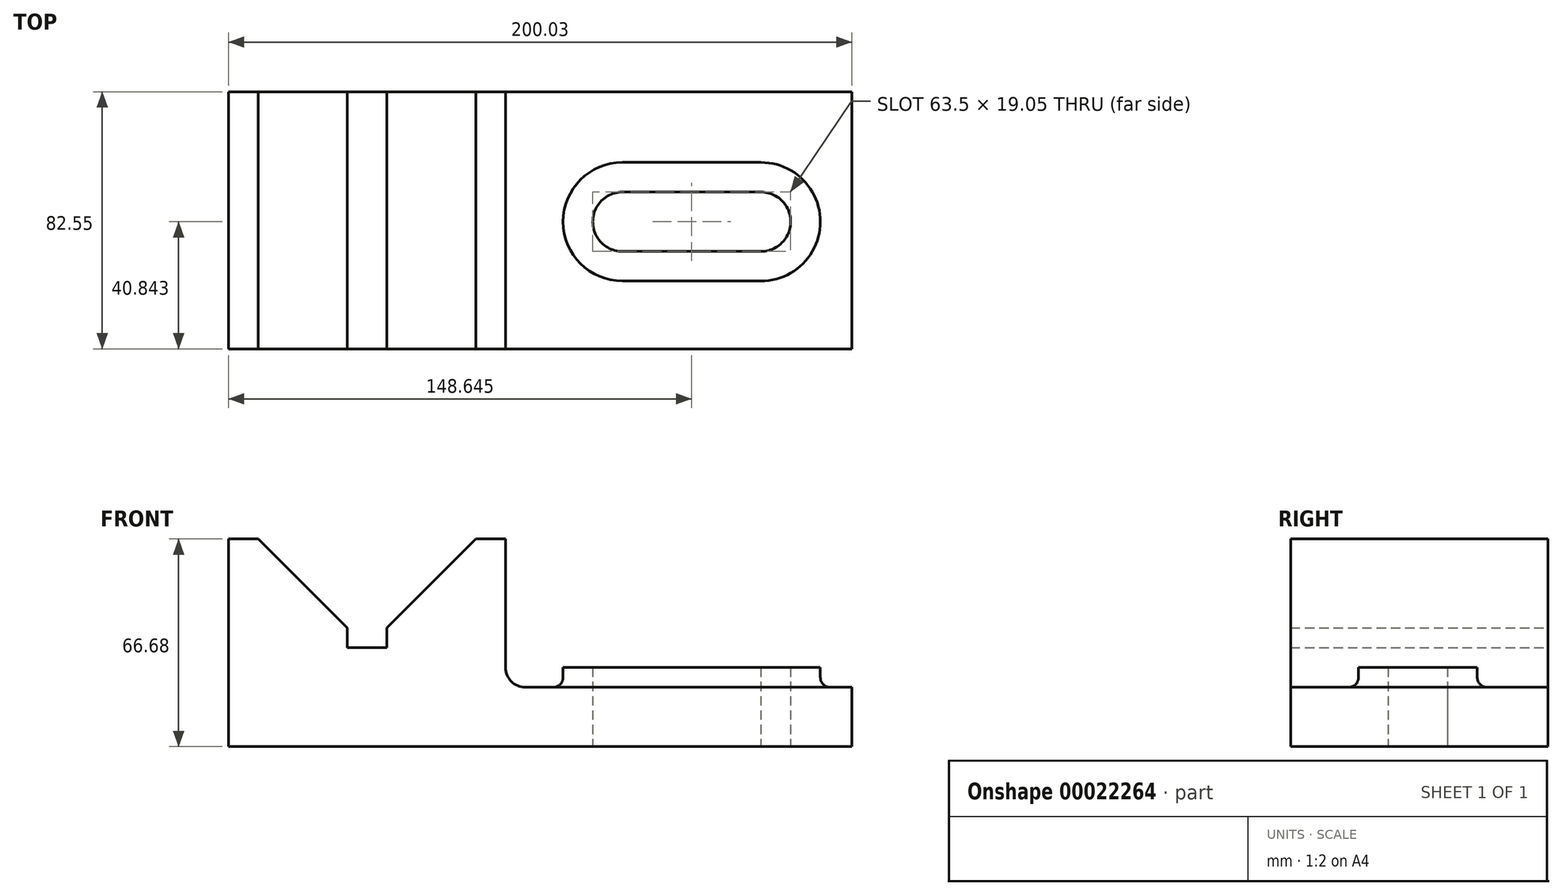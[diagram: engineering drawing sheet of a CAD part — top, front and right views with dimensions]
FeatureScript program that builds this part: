
annotation { "Feature Type Name" : "Feature", "Feature Type Description" : "" }
export const myFeature = defineFeature(function(context is Context, id is Id, definition is map)
    precondition{}
    {
        {
            var Q0;
            Q0=qCreatedBy(makeId("Front.planeOp"),FACE);
            var sketch = newSketch(context, id + "F0", { "sketchPlane" : qUnion([Q0])});
            skLineSegment(sketch, "E0.bottom", {"start": v(0, 0) * mm, "end": v(-200.03, 0) * mm});
            skLineSegment(sketch, "E0.left", {"start": v(0, 0) * mm, "end": v(0, 19.05) * mm});
            skLineSegment(sketch, "E0.right", {"start": v(-200.03, 0) * mm, "end": v(-200.03, 66.68) * mm});
            skLineSegment(sketch, "E1", {"start": v(-111.12, 66.68) * mm, "end": v(-111.12, 25.4) * mm});
            skLineSegment(sketch, "E2", {"start": v(-104.77, 19.05) * mm, "end": v(0, 19.05) * mm});
            skPoint(sketch, "E3.orphan", {"position": v(0, 57.15) * mm});
            skArc(sketch, "E4", {"start": v(-111.12, 25.4) * mm, "mid": v(-109.27, 20.9) * mm, "end": v(-104.77, 19.05) * mm});
            skLineSegment(sketch, "E5", {"start": v(-200.03, 66.68) * mm, "end": v(-190.5, 66.68) * mm});
            skLineSegment(sketch, "E6", {"start": v(-190.5, 66.68) * mm, "end": v(-161.93, 38.1) * mm});
            skLineSegment(sketch, "E7", {"start": v(-120.65, 66.68) * mm, "end": v(-149.23, 38.1) * mm});
            skLineSegment(sketch, "E8", {"start": v(-155.58, 31.75) * mm, "end": v(-149.23, 31.75) * mm});
            skLineSegment(sketch, "E9", {"start": v(-149.23, 31.75) * mm, "end": v(-161.93, 31.75) * mm});
            skLineSegment(sketch, "E10", {"start": v(-161.93, 31.75) * mm, "end": v(-161.93, 38.1) * mm});
            skLineSegment(sketch, "E11", {"start": v(-149.23, 31.75) * mm, "end": v(-149.23, 38.1) * mm});
            skLineSegment(sketch, "E12.trimOffspring", {"start": v(-120.65, 66.68) * mm, "end": v(-111.12, 66.68) * mm});
            skSolve(sketch);
        }
        {
            var Q0;
            Q0 = qSketchRegion(id + "F0", true);
            var Q1;
            Q1=makeQuery(id+"F0.imprint","IMPRINT",FACE,{"disambiguationData":[TD([[makeQuery(id+"F0.imprint","IMPRINT",EDGE,{"derivedFrom":sQuery(id+"F0.wireOp",EDGE,"E0.bottom")}),-1.0]])]});
            extrude(context, id + "F1", {"entities" : qUnion([Q0, Q1]), "depth" : 82.55 * mm});
        }
        {
            var Q0;
            Q0=makeQuery(id+"F1.opExtrude","SWEPT_FACE",FACE,{"disambiguationData":[OSD([sQuery(id+"F0.wireOp",EDGE,"E2")])]});
            var sketch = newSketch(context, id + "F2", { "sketchPlane" : qUnion([Q0])});
            skArc(sketch, "E13", {"start": v(-73.6, -22.66) * mm, "mid": v(-92.66, -41.7) * mm, "end": v(-73.6, -60.76) * mm});
            skPoint(sketch, "E14.center.orphan", {"position": v(-29.16, -41.7) * mm});
            skArc(sketch, "E15", {"start": v(-29.16, -60.76) * mm, "mid": v(-10.1, -41.7) * mm, "end": v(-29.16, -22.66) * mm});
            skLineSegment(sketch, "E16", {"start": v(-29.16, -60.76) * mm, "end": v(-73.6, -60.76) * mm});
            skLineSegment(sketch, "E17", {"start": v(-73.6, -22.66) * mm, "end": v(-29.16, -22.66) * mm});
            skArc(sketch, "E18", {"start": v(-73.6, -32.18) * mm, "mid": v(-83.13, -41.73) * mm, "end": v(-73.57, -51.23) * mm});
            skArc(sketch, "E19", {"start": v(-29.2, -51.23) * mm, "mid": v(-19.63, -41.68) * mm, "end": v(-29.26, -32.18) * mm});
            skLineSegment(sketch, "E20", {"start": v(-29.2, -51.23) * mm, "end": v(-73.65, -51.23) * mm});
            skLineSegment(sketch, "E21", {"start": v(-29.05, -32.18) * mm, "end": v(-73.6, -32.18) * mm});
            skPoint(sketch, "E22.trimOffspring.end.orphan", {"position": v(-104.78, -41.7) * mm});
            skPoint(sketch, "E23.start.orphan", {"position": v(0, -41.28) * mm});
            skSolve(sketch);
        }
        {
            var Q0;
            Q0=makeQuery(id+"F2.imprint","IMPRINT",FACE,{"disambiguationData":[TD([[makeQuery(id+"F2.imprint","IMPRINT",EDGE,{"derivedFrom":sQuery(id+"F2.wireOp",EDGE,"E13")}),1.0]])]});
            extrude(context, id + "F3", {"entities" : qUnion([Q0]), "operationType" : NewBodyOperationType.ADD, "depth" : 6.35 * mm});
        }
        {
            var Q0;
            Q0=makeQuery(id+"F3.opExtrude","CAP_EDGE",EDGE,{"disambiguationData":[OSD([sQuery(id+"F2.wireOp",EDGE,"E15")])],"isStart":true});
            fillet(context, id + "F4", {"entities" : qUnion([Q0]), "radius" : 3.17 * mm, "tangentPropagation" : true, "allowEdgeOverflow" : false});
        }
        {
            var Q0;
            Q0=makeQuery(id+"F3.boolean.opBoolean","SPLIT",FACE,{"disambiguationData":[TD([makeQuery(id+"F3.opExtrude","SWEPT_FACE",FACE,{"disambiguationData":[OSD([sQuery(id+"F2.wireOp",EDGE,"E18")])]})])],"derivedFrom":makeQuery(id+"F1.opExtrude","SWEPT_FACE",FACE,{"disambiguationData":[OSD([sQuery(id+"F0.wireOp",EDGE,"E2")])]})});
            extrude(context, id + "F5", {"entities" : qUnion([Q0]), "operationType" : NewBodyOperationType.REMOVE, "oppositeDirection" : true, "depth" : 25.4 * mm});
        }
    });
